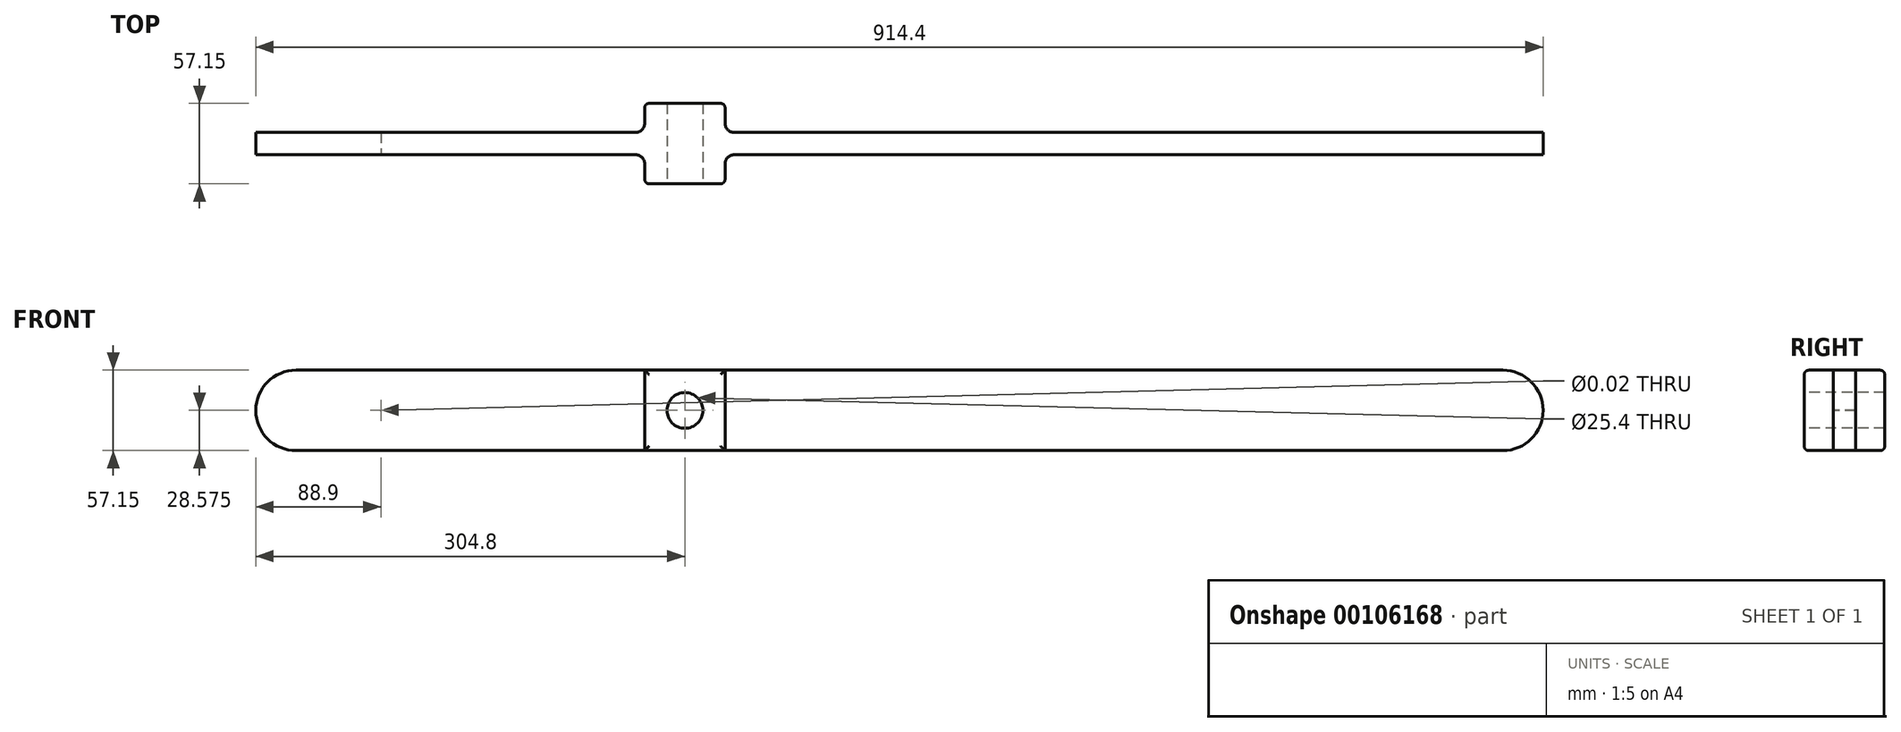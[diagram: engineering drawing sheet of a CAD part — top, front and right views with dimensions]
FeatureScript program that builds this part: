
annotation { "Feature Type Name" : "Feature", "Feature Type Description" : "" }
export const myFeature = defineFeature(function(context is Context, id is Id, definition is map)
    precondition{}
    {
        {
            var Q0;
            Q0=qCreatedBy(makeId("Top.planeOp"),FACE);
            var sketch = newSketch(context, id + "F0", { "sketchPlane" : qUnion([Q0])});
            skLineSegment(sketch, "E0", {"start": v(34.92, 0) * mm, "end": v(609.6, 0) * mm});
            skLineSegment(sketch, "E1", {"start": v(-34.93, 0) * mm, "end": v(-304.8, 0) * mm});
            skLineSegment(sketch, "E2.0", {"start": v(34.92, 15.88) * mm, "end": v(609.6, 15.88) * mm});
            skLineSegment(sketch, "E3.0", {"start": v(-34.93, 15.88) * mm, "end": v(-304.8, 15.87) * mm});
            skLineSegment(sketch, "E4", {"start": v(-304.8, 15.87) * mm, "end": v(-304.8, 0) * mm});
            skLineSegment(sketch, "E5", {"start": v(609.6, 15.88) * mm, "end": v(609.6, 0) * mm});
            skLineSegment(sketch, "E6.0", {"start": v(0, -20.64) * mm, "end": v(28.58, -20.64) * mm});
            skLineSegment(sketch, "E7.0", {"start": v(0, 36.51) * mm, "end": v(28.58, 36.51) * mm});
            skLineSegment(sketch, "E8.0", {"start": v(-28.58, 36.51) * mm, "end": v(-28.58, 22.23) * mm});
            skLineSegment(sketch, "E9.0", {"start": v(28.58, 36.51) * mm, "end": v(28.58, 22.23) * mm});
            skLineSegment(sketch, "E10", {"start": v(-28.58, 36.51) * mm, "end": v(0, 36.51) * mm});
            skLineSegment(sketch, "E11", {"start": v(-28.58, -20.64) * mm, "end": v(0, -20.64) * mm});
            skLineSegment(sketch, "E12.trimOffspring", {"start": v(28.58, -6.35) * mm, "end": v(28.58, -20.64) * mm});
            skLineSegment(sketch, "E13.trimOffspring", {"start": v(-28.58, -6.35) * mm, "end": v(-28.58, -20.64) * mm});
            skPoint(sketch, "E14.visualSharp", {"position": v(28.58, 0) * mm});
            skArc(sketch, "E14.filletArc", {"start": v(34.92, 0) * mm, "mid": v(30.43, -1.86) * mm, "end": v(28.58, -6.35) * mm});
            skPoint(sketch, "E15.visualSharp", {"position": v(28.58, 15.88) * mm});
            skArc(sketch, "E15.filletArc", {"start": v(28.58, 22.23) * mm, "mid": v(30.43, 17.73) * mm, "end": v(34.92, 15.87) * mm});
            skPoint(sketch, "E16.visualSharp", {"position": v(-28.58, 15.88) * mm});
            skArc(sketch, "E16.filletArc", {"start": v(-34.93, 15.88) * mm, "mid": v(-30.43, 17.73) * mm, "end": v(-28.58, 22.23) * mm});
            skPoint(sketch, "E17.visualSharp", {"position": v(-28.58, 0) * mm});
            skArc(sketch, "E17.filletArc", {"start": v(-28.57, -6.35) * mm, "mid": v(-30.43, -1.86) * mm, "end": v(-34.93, 0) * mm});
            skSolve(sketch);
        }
        {
            var Q0;
            Q0=makeQuery(id+"F0.imprint","IMPRINT",FACE,{"disambiguationData":[TD([[makeQuery(id+"F0.imprint","IMPRINT",EDGE,{"derivedFrom":sQuery(id+"F0.wireOp",EDGE,"E0")}),1.0]])]});
            extrude(context, id + "F1", {"entities" : qUnion([Q0]), "depth" : 57.15 * mm});
        }
        {
            var Q0;
            Q0=makeQuery(id+"F1.opExtrude","SWEPT_FACE",FACE,{"disambiguationData":[OSD([sQuery(id+"F0.wireOp",EDGE,"E7.0"),sQuery(id+"F0.wireOp",EDGE,"E10")])]});
            var Q1;
            Q1=makeQuery(id+"F1.opExtrude","SWEPT_FACE",FACE,{"disambiguationData":[OSD([sQuery(id+"F0.wireOp",EDGE,"E6.0"),sQuery(id+"F0.wireOp",EDGE,"E11")])]});
            fillet(context, id + "F2", {"entities" : qUnion([Q0, Q1]), "radius" : 3.17 * mm, "tangentPropagation" : true, "allowEdgeOverflow" : false});
        }
        {
            var Q0;
            Q0=makeQuery(id+"F1.opExtrude","CAP_EDGE",EDGE,{"disambiguationData":[OSD([sQuery(id+"F0.wireOp",EDGE,"E4")])],"isStart":false});
            var Q1;
            Q1=makeQuery(id+"F1.opExtrude","CAP_EDGE",EDGE,{"disambiguationData":[OSD([sQuery(id+"F0.wireOp",EDGE,"E4")])],"isStart":true});
            fillet(context, id + "F3", {"entities" : qUnion([Q0, Q1]), "radius" : 28.57 * mm, "tangentPropagation" : true, "allowEdgeOverflow" : false});
        }
        {
            var Q0;
            Q0=makeQuery(id+"F1.opExtrude","CAP_EDGE",EDGE,{"disambiguationData":[OSD([sQuery(id+"F0.wireOp",EDGE,"E5")])],"isStart":false});
            fillet(context, id + "F4", {"entities" : qUnion([Q0]), "radius" : 28.57 * mm, "tangentPropagation" : true, "allowEdgeOverflow" : false});
        }
        {
            var Q0;
            Q0=makeQuery(id+"F1.opExtrude","CAP_EDGE",EDGE,{"disambiguationData":[OSD([sQuery(id+"F0.wireOp",EDGE,"E5")])],"isStart":true});
            fillet(context, id + "F5", {"entities" : qUnion([Q0]), "radius" : 28.57 * mm, "tangentPropagation" : true, "allowEdgeOverflow" : false});
        }
        {
            var Q0;
            Q0=qCreatedBy(makeId("Front.planeOp"),FACE);
            var sketch = newSketch(context, id + "F6", { "sketchPlane" : qUnion([Q0])});
            skLineSegment(sketch, "E18", {"start": v(0, 0) * mm, "end": v(0, 57.15) * mm});
            skCircle(sketch, "E19", {"center": v(0, 28.58) * mm, "radius": 12.7 * mm});
            skLineSegment(sketch, "E20", {"start": v(0, 28.58) * mm, "end": v(-215.9, 28.58) * mm});
            skSolve(sketch);
        }
        {
            var Q0;
            Q0=sQuery(id+"F6.wireOp",VERTEX,"E20.end");
            var Q1;
            Q1=makeQuery(id+"F1.opExtrude","SWEPT_BODY",BODY,{"disambiguationData":[OSD([sQuery(id+"F0.wireOp",EDGE,"E0"),sQuery(id+"F0.wireOp",EDGE,"E1"),sQuery(id+"F0.wireOp",EDGE,"E2.0"),sQuery(id+"F0.wireOp",EDGE,"E3.0"),sQuery(id+"F0.wireOp",EDGE,"E4"),sQuery(id+"F0.wireOp",EDGE,"E5"),sQuery(id+"F0.wireOp",EDGE,"E6.0"),sQuery(id+"F0.wireOp",EDGE,"E7.0"),sQuery(id+"F0.wireOp",EDGE,"E8.0"),sQuery(id+"F0.wireOp",EDGE,"E9.0"),sQuery(id+"F0.wireOp",EDGE,"E10"),sQuery(id+"F0.wireOp",EDGE,"E11"),sQuery(id+"F0.wireOp",EDGE,"E12.trimOffspring"),sQuery(id+"F0.wireOp",EDGE,"E13.trimOffspring"),sQuery(id+"F0.wireOp",EDGE,"E14.filletArc"),sQuery(id+"F0.wireOp",EDGE,"E15.filletArc"),sQuery(id+"F0.wireOp",EDGE,"E16.filletArc"),sQuery(id+"F0.wireOp",EDGE,"E17.filletArc")])]});
            hole(context, id + "F7", {"style" : HoleStyle.SIMPLE, "holeDiameter" : 5 / 203.2 * mm, "endStyle" : HoleEndStyle.THROUGH, "locations" : qUnion([Q0]), "scope" : qUnion([Q1])});
        }
        {
            var Q0;
            Q0=sQuery(id+"F6.wireOp",VERTEX,"E19.center");
            var Q1;
            Q1=makeQuery(id+"F1.opExtrude","SWEPT_BODY",BODY,{"disambiguationData":[OSD([sQuery(id+"F0.wireOp",EDGE,"E0"),sQuery(id+"F0.wireOp",EDGE,"E1"),sQuery(id+"F0.wireOp",EDGE,"E2.0"),sQuery(id+"F0.wireOp",EDGE,"E3.0"),sQuery(id+"F0.wireOp",EDGE,"E4"),sQuery(id+"F0.wireOp",EDGE,"E5"),sQuery(id+"F0.wireOp",EDGE,"E6.0"),sQuery(id+"F0.wireOp",EDGE,"E7.0"),sQuery(id+"F0.wireOp",EDGE,"E8.0"),sQuery(id+"F0.wireOp",EDGE,"E9.0"),sQuery(id+"F0.wireOp",EDGE,"E10"),sQuery(id+"F0.wireOp",EDGE,"E11"),sQuery(id+"F0.wireOp",EDGE,"E12.trimOffspring"),sQuery(id+"F0.wireOp",EDGE,"E13.trimOffspring"),sQuery(id+"F0.wireOp",EDGE,"E14.filletArc"),sQuery(id+"F0.wireOp",EDGE,"E15.filletArc"),sQuery(id+"F0.wireOp",EDGE,"E16.filletArc"),sQuery(id+"F0.wireOp",EDGE,"E17.filletArc")])]});
            hole(context, id + "F8", {"style" : HoleStyle.SIMPLE, "holeDiameter" : 25.4 * mm, "endStyle" : HoleEndStyle.BLIND, "holeDepth" : 38.1 * mm, "locations" : qUnion([Q0]), "scope" : qUnion([Q1])});
        }
        {
            var Q0;
            Q0=sQuery(id+"F6.wireOp",VERTEX,"E19.center");
            var Q1;
            Q1=makeQuery(id+"F1.opExtrude","SWEPT_BODY",BODY,{"disambiguationData":[OSD([sQuery(id+"F0.wireOp",EDGE,"E0"),sQuery(id+"F0.wireOp",EDGE,"E1"),sQuery(id+"F0.wireOp",EDGE,"E2.0"),sQuery(id+"F0.wireOp",EDGE,"E3.0"),sQuery(id+"F0.wireOp",EDGE,"E4"),sQuery(id+"F0.wireOp",EDGE,"E5"),sQuery(id+"F0.wireOp",EDGE,"E6.0"),sQuery(id+"F0.wireOp",EDGE,"E7.0"),sQuery(id+"F0.wireOp",EDGE,"E8.0"),sQuery(id+"F0.wireOp",EDGE,"E9.0"),sQuery(id+"F0.wireOp",EDGE,"E10"),sQuery(id+"F0.wireOp",EDGE,"E11"),sQuery(id+"F0.wireOp",EDGE,"E12.trimOffspring"),sQuery(id+"F0.wireOp",EDGE,"E13.trimOffspring"),sQuery(id+"F0.wireOp",EDGE,"E14.filletArc"),sQuery(id+"F0.wireOp",EDGE,"E15.filletArc"),sQuery(id+"F0.wireOp",EDGE,"E16.filletArc"),sQuery(id+"F0.wireOp",EDGE,"E17.filletArc")])]});
            hole(context, id + "F9", {"style" : HoleStyle.SIMPLE, "holeDiameter" : 25.4 * mm, "endStyle" : HoleEndStyle.THROUGH, "oppositeDirection" : true, "locations" : qUnion([Q0]), "scope" : qUnion([Q1])});
        }
    });
